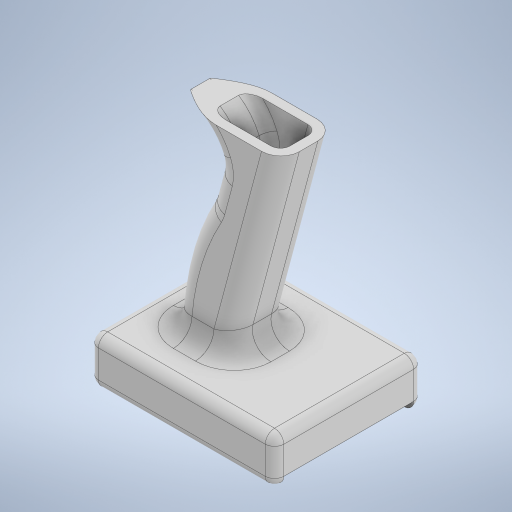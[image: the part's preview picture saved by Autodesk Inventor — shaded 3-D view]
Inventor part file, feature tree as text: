
AUTODESK INVENTOR PART (.ipt)
format: ipt  version: 2023.2 (Build 272271030, 271C)  size: 484,864 bytes
history: native  units: mm
features: sketch x8, extrude x5, fillet x4, projected_geometry x2, shell x1
ambient origin geometry x8: Origin, YZ Plane, XZ Plane, XY Plane, X Axis, Y Axis, Z Axis, Center Point
bodies: Solid1 (feature_tree)
feature tree (20):
  extrude  "Extrusion1"  Depth=80.0mm
  fillet  "Fillet1"  Radius=25.0mm
  extrude  "Extrusion2"  Depth=62.0mm
  extrude  "Extrusion3"  Depth=10.0mm TaperAngle=0.0deg
  extrude  "Extrusion4"  Depth=30.0mm TaperAngle=0.0deg
  sketch  "Sketch7"  dims[d34=75.0deg d35=70.0mm d36=140.0mm d37=25.0mm d38=10.0mm d39=10.0mm]
  extrude  "Extrusion7"  Depth=70.0mm
  sketch  "Sketch9"  dims[d41=5.0mm]
  fillet  "Fillet2"  Radius=140.0mm
  fillet  "Fillet3"  Radius=25.0mm
  fillet  "Fillet4"  Radius=10.0mm
  shell  "Shell1"  Thickness=10.0mm
  sketch  "Sketch15"
  sketch  "Sketch1"  dims[d0=100.0mm d1=80.0mm d2=25.0mm d3=0.0mm]
  sketch  "Sketch2"  dims[d4=5.0mm d5=62.0mm]
  projected_geometry  "Projected Loop1"
  sketch  "Sketch3"  dims[d6=75.0mm d7=0.0mm d8=10.0mm d9=0.0mm]
  projected_geometry  "Projected Loop2"
  sketch  "Sketch4"  dims[d10=70.0mm d11=0.0mm d26=30.0mm d27=0.0mm]
  sketch  "Sketch8"  dims[d40=10.0mm]
